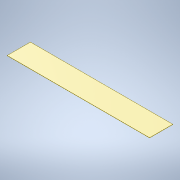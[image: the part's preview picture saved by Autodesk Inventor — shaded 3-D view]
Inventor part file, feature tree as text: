
AUTODESK INVENTOR PART (.ipt)
format: ipt  version: 2021 (Build 250183000, 183)  size: 93,184 bytes
history: native  units: mm
features: extrude x1, sketch x1
ambient origin geometry x8: Origin, YZ Plane, XZ Plane, XY Plane, X Axis, Y Axis, Z Axis, Center Point
bodies: Solid1 (feature_tree)
feature tree (2):
  extrude  "Extrusion1"  Depth=2000.0mm
  sketch  "Sketch1"  dims[d0=326.0mm d1=2000.0mm d2=3.0mm d3=0.0mm]
